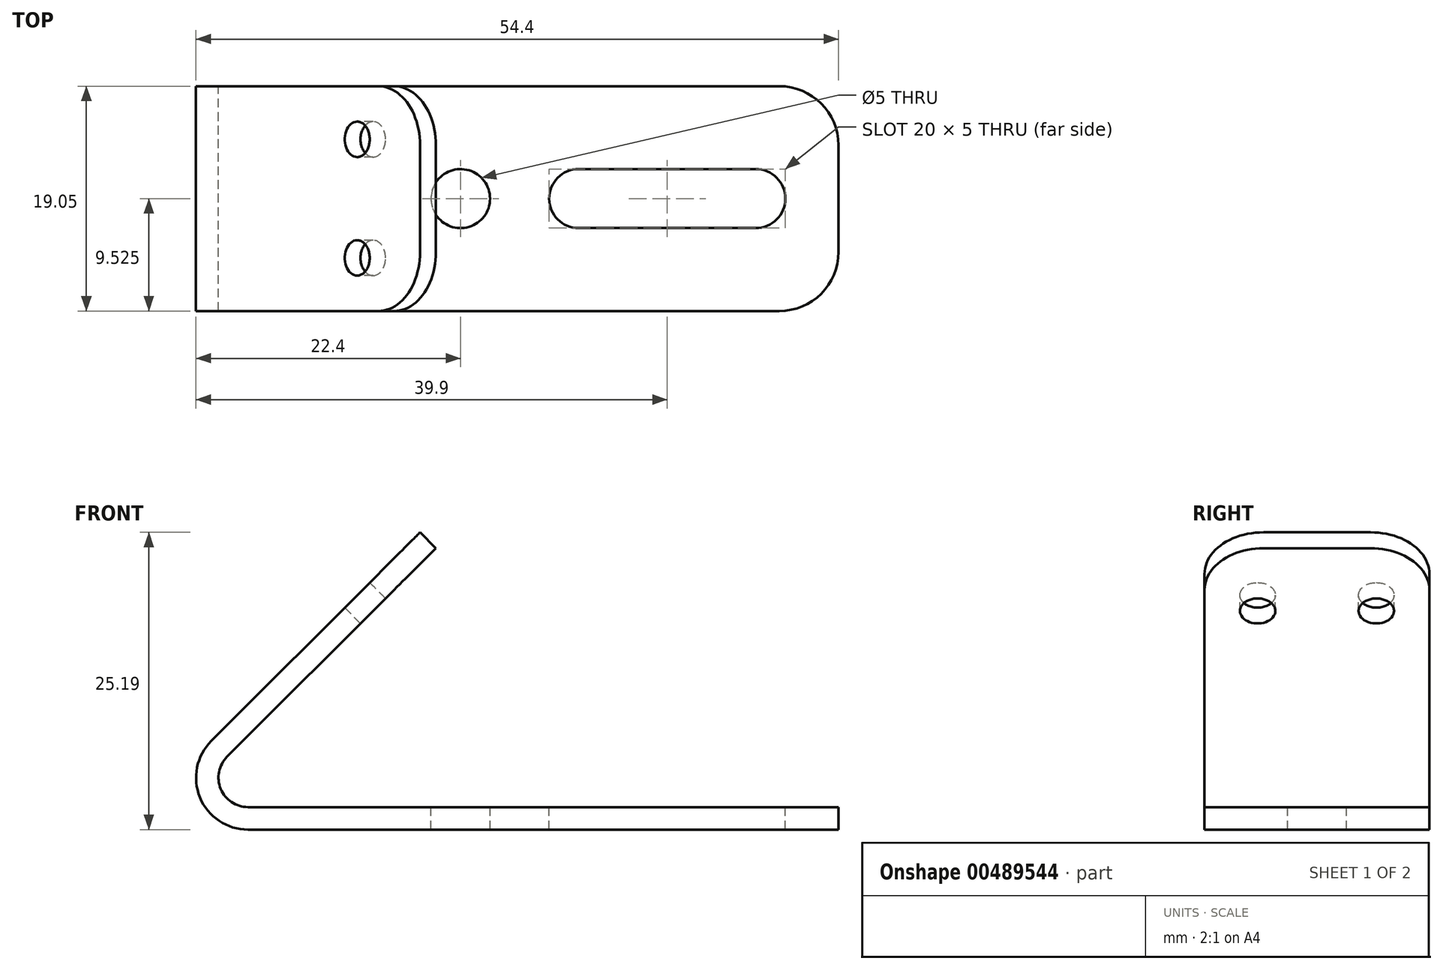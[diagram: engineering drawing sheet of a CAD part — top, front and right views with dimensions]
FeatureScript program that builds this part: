
annotation { "Feature Type Name" : "Feature", "Feature Type Description" : "" }
export const myFeature = defineFeature(function(context is Context, id is Id, definition is map)
    precondition{}
    {
        {
            var Q0;
            Q0=qCreatedBy(makeId("Front.planeOp"),FACE);
            var sketch = newSketch(context, id + "F0", { "sketchPlane" : qUnion([Q0])});
            skLineSegment(sketch, "E0", {"start": v(0, 0) * mm, "end": v(-50, 0) * mm});
            skLineSegment(sketch, "E1", {"start": v(-53.11, 7.51) * mm, "end": v(-35.43, 25.19) * mm});
            skPoint(sketch, "E2.visualSharp", {"position": v(-60.62, 0) * mm});
            skArc(sketch, "E2.filletArc", {"start": v(-53.11, 7.51) * mm, "mid": v(-54.07, 2.72) * mm, "end": v(-50, 0) * mm});
            skLineSegment(sketch, "E3.0", {"start": v(0, 1.9) * mm, "end": v(-50, 1.9) * mm});
            skArc(sketch, "E3.1", {"start": v(-51.77, 6.17) * mm, "mid": v(-52.3, 3.44) * mm, "end": v(-50, 1.9) * mm});
            skLineSegment(sketch, "E3.2", {"start": v(-51.77, 6.17) * mm, "end": v(-34.1, 23.85) * mm});
            skLineSegment(sketch, "E4", {"start": v(-35.43, 25.19) * mm, "end": v(-34.1, 23.85) * mm});
            skLineSegment(sketch, "E5", {"start": v(0, 1.9) * mm, "end": v(0, 0) * mm});
            skSolve(sketch);
        }
        {
            var Q0;
            Q0 = qSketchRegion(id + "F0", true);
            extrude(context, id + "F1", {"entities" : qUnion([Q0]), "depth" : 19.05 * mm});
        }
        {
            var Q0;
            Q0=makeQuery(id+"F1.opExtrude","CAP_EDGE",EDGE,{"disambiguationData":[OSD([sQuery(id+"F0.wireOp",EDGE,"E4")])],"isStart":false});
            var Q1;
            Q1=makeQuery(id+"F1.opExtrude","CAP_EDGE",EDGE,{"disambiguationData":[OSD([sQuery(id+"F0.wireOp",EDGE,"E4")])],"isStart":true});
            var Q2;
            Q2=makeQuery(id+"F1.opExtrude","CAP_EDGE",EDGE,{"disambiguationData":[OSD([sQuery(id+"F0.wireOp",EDGE,"E5")])],"isStart":true});
            var Q3;
            Q3=makeQuery(id+"F1.opExtrude","CAP_EDGE",EDGE,{"disambiguationData":[OSD([sQuery(id+"F0.wireOp",EDGE,"E5")])],"isStart":false});
            fillet(context, id + "F2", {"entities" : qUnion([Q0, Q1, Q2, Q3]), "radius" : 5 * mm, "tangentPropagation" : true, "allowEdgeOverflow" : false});
        }
        {
            var Q0;
            Q0=makeQuery(id+"F1.opExtrude","SWEPT_FACE",FACE,{"disambiguationData":[OSD([sQuery(id+"F0.wireOp",EDGE,"E1")])]});
            var sketch = newSketch(context, id + "F3", { "sketchPlane" : qUnion([Q0])});
            skLineSegment(sketch, "E6.0", {"start": v(14.05, -7.24) * mm, "end": v(5, -7.24) * mm, "construction": true});
            skLineSegment(sketch, "E7.0", {"start": v(19.05, -32.24) * mm, "end": v(19.05, -12.24) * mm});
            skLineSegment(sketch, "E8.0", {"start": v(19.05, -32.24) * mm, "end": v(0, -32.24) * mm});
            skLineSegment(sketch, "E9.0", {"start": v(0, -32.24) * mm, "end": v(0, -12.24) * mm});
            skCircle(sketch, "E10", {"center": v(14.55, -14.77) * mm, "radius": 1.5 * mm});
            skCircle(sketch, "E11", {"center": v(4.5, -14.77) * mm, "radius": 1.5 * mm});
            skLineSegment(sketch, "E12", {"start": v(19.05, -14.77) * mm, "end": v(14.55, -14.77) * mm});
            skLineSegment(sketch, "E13", {"start": v(14.55, -14.77) * mm, "end": v(14.55, -7.27) * mm, "construction": true});
            skLineSegment(sketch, "E14", {"start": v(14.55, -14.77) * mm, "end": v(0, -14.77) * mm, "construction": true});
            skSolve(sketch);
        }
        {
            var Q0;
            Q0 = qSketchRegion(id + "F3", true);
            extrude(context, id + "F4", {"entities" : qUnion([Q0]), "operationType" : NewBodyOperationType.REMOVE, "endBound" : BoundingType.UP_TO_NEXT, "oppositeDirection" : true, "depth" : 25 * mm});
        }
        {
            var Q0;
            Q0=makeQuery(id+"F1.opExtrude","SWEPT_FACE",FACE,{"disambiguationData":[OSD([sQuery(id+"F0.wireOp",EDGE,"E3.0")])]});
            var sketch = newSketch(context, id + "F5", { "sketchPlane" : qUnion([Q0])});
            skPoint(sketch, "E15.0", {"position": v(0, -9.53) * mm});
            skLineSegment(sketch, "E16.0", {"start": v(-50, -19.05) * mm, "end": v(-50, 0) * mm});
            skLineSegment(sketch, "E17", {"start": v(0, -9.53) * mm, "end": v(-50, -9.53) * mm, "construction": true});
            skPoint(sketch, "E18", {"position": v(-32, -9.53) * mm});
            skCircle(sketch, "E19", {"center": v(-32, -9.53) * mm, "radius": 2.5 * mm});
            skPoint(sketch, "E20", {"position": v(-4.5, -9.53) * mm});
            skLineSegment(sketch, "E21.bottom", {"start": v(-7, -7.03) * mm, "end": v(-22, -7.03) * mm});
            skLineSegment(sketch, "E21.top", {"start": v(-7, -12.03) * mm, "end": v(-22, -12.03) * mm});
            skPoint(sketch, "E21.middle", {"position": v(-14.5, -9.53) * mm});
            skArc(sketch, "E22", {"start": v(-22, -7.03) * mm, "mid": v(-24.5, -9.53) * mm, "end": v(-22, -12.03) * mm});
            skArc(sketch, "E23", {"start": v(-7, -12.03) * mm, "mid": v(-4.5, -9.53) * mm, "end": v(-7, -7.03) * mm});
            skSolve(sketch);
        }
        {
            var Q0;
            Q0=makeQuery(id+"F5.imprint","IMPRINT",FACE,{"disambiguationData":[TD([[makeQuery(id+"F5.imprint","IMPRINT",EDGE,{"derivedFrom":sQuery(id+"F5.wireOp",EDGE,"E21.bottom")}),1.0]])]});
            var Q1;
            Q1=makeQuery(id+"F5.imprint","IMPRINT",FACE,{"disambiguationData":[TD([[makeQuery(id+"F5.imprint","IMPRINT",EDGE,{"derivedFrom":sQuery(id+"F5.wireOp",EDGE,"E19")}),1.0]])]});
            extrude(context, id + "F6", {"entities" : qUnion([Q0, Q1]), "operationType" : NewBodyOperationType.REMOVE, "endBound" : BoundingType.THROUGH_ALL, "oppositeDirection" : true, "depth" : 25 * mm});
        }
    });
